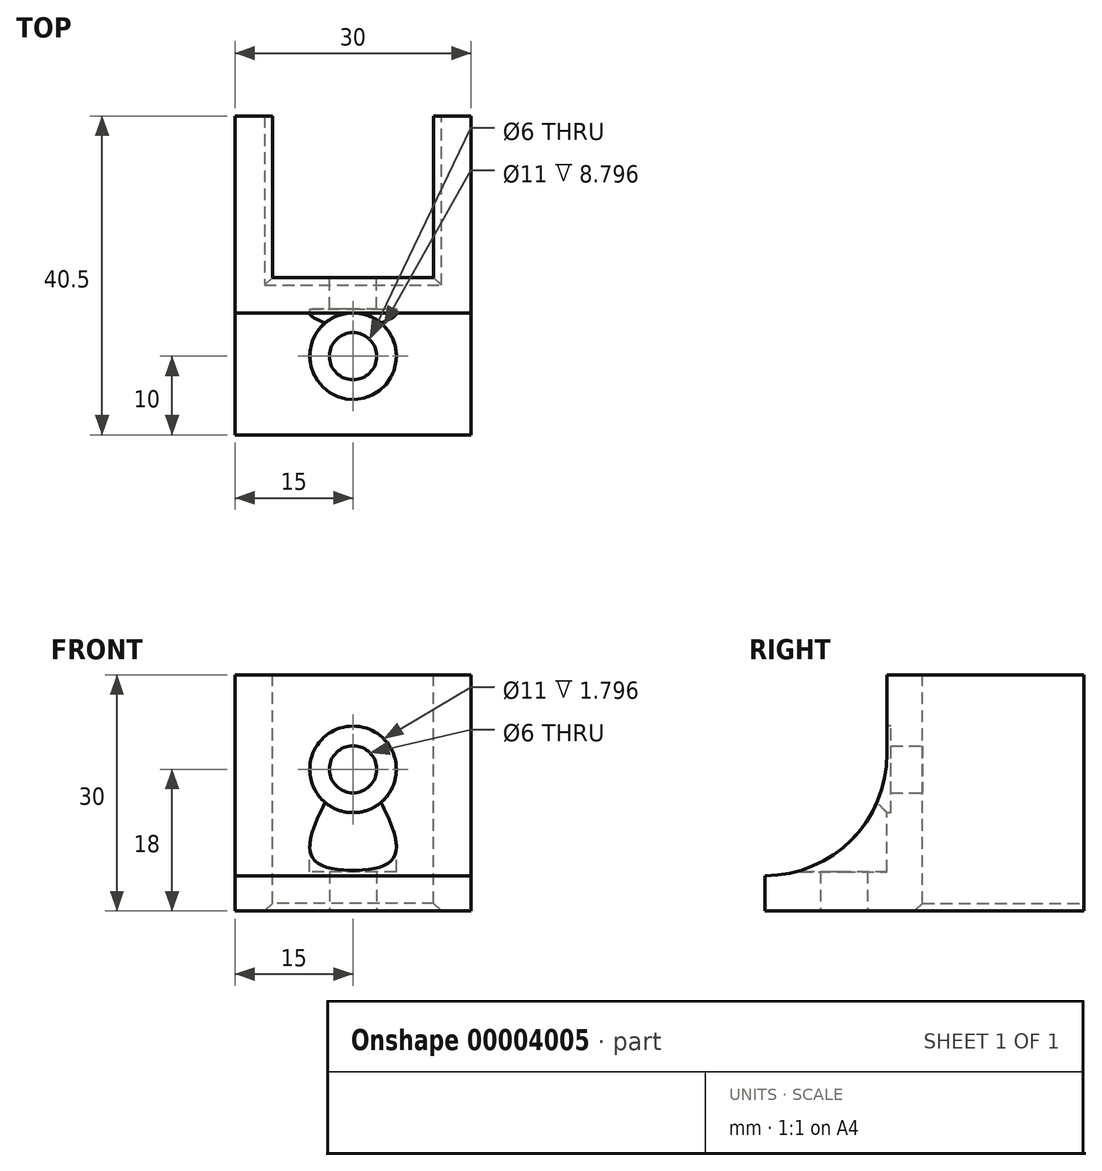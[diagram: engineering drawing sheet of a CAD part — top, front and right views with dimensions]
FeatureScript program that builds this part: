
annotation { "Feature Type Name" : "Feature", "Feature Type Description" : "" }
export const myFeature = defineFeature(function(context is Context, id is Id, definition is map)
    precondition{}
    {
        {
            var Q0;
            Q0=qCreatedBy(makeId("Top.planeOp"),FACE);
            var sketch = newSketch(context, id + "F0", { "sketchPlane" : qUnion([Q0])});
            skLineSegment(sketch, "E0", {"start": v(-15, 0) * mm, "end": v(15, 0) * mm});
            skLineSegment(sketch, "E1", {"start": v(15, 0) * mm, "end": v(15, 40.5) * mm});
            skLineSegment(sketch, "E2", {"start": v(15, 40.5) * mm, "end": v(-15, 40.5) * mm});
            skLineSegment(sketch, "E3", {"start": v(-15, 40.5) * mm, "end": v(-15, 0) * mm});
            skSolve(sketch);
        }
        {
            var Q0;
            Q0=makeQuery(id+"F0.imprint","IMPRINT",FACE,{"disambiguationData":[TD([[makeQuery(id+"F0.imprint","IMPRINT",EDGE,{"derivedFrom":sQuery(id+"F0.wireOp",EDGE,"E0")}),1.0]])]});
            extrude(context, id + "F1", {"entities" : qUnion([Q0]), "depth" : 30 * mm});
        }
        {
            var Q0;
            Q0=makeQuery(id+"F1.opExtrude","CAP_FACE",FACE,{"disambiguationData":[OSD([sQuery(id+"F0.wireOp",EDGE,"E0"),sQuery(id+"F0.wireOp",EDGE,"E1"),sQuery(id+"F0.wireOp",EDGE,"E2"),sQuery(id+"F0.wireOp",EDGE,"E3")])],"isStart":false});
            var sketch = newSketch(context, id + "F2", { "sketchPlane" : qUnion([Q0])});
            skLineSegment(sketch, "E4.bottom", {"start": v(-10.25, 40.5) * mm, "end": v(10.25, 40.5) * mm});
            skLineSegment(sketch, "E4.top", {"start": v(-10.25, 20) * mm, "end": v(10.25, 20) * mm});
            skLineSegment(sketch, "E4.left", {"start": v(-10.25, 40.5) * mm, "end": v(-10.25, 20) * mm});
            skLineSegment(sketch, "E4.right", {"start": v(10.25, 40.5) * mm, "end": v(10.25, 20) * mm});
            skLineSegment(sketch, "E5", {"start": v(0, 0) * mm, "end": v(0, 20) * mm, "construction": true});
            skSolve(sketch);
        }
        {
            var Q0;
            Q0=makeQuery(id+"F2.imprint","IMPRINT",FACE,{"disambiguationData":[TD([[makeQuery(id+"F2.imprint","IMPRINT",EDGE,{"derivedFrom":sQuery(id+"F2.wireOp",EDGE,"E4.bottom")}),1.0]])]});
            extrude(context, id + "F3", {"entities" : qUnion([Q0]), "operationType" : NewBodyOperationType.REMOVE, "endBound" : BoundingType.THROUGH_ALL, "oppositeDirection" : true, "depth" : 25 * mm});
        }
        {
            var Q0;
            Q0=makeQuery(id+"F1.opExtrude","CAP_FACE",FACE,{"disambiguationData":[OSD([sQuery(id+"F0.wireOp",EDGE,"E0"),sQuery(id+"F0.wireOp",EDGE,"E1"),sQuery(id+"F0.wireOp",EDGE,"E2"),sQuery(id+"F0.wireOp",EDGE,"E3")])],"isStart":true});
            var sketch = newSketch(context, id + "F4", { "sketchPlane" : qUnion([Q0])});
            skLineSegment(sketch, "E6", {"start": v(0, 0) * mm, "end": v(0, -10) * mm, "construction": true});
            skCircle(sketch, "E7", {"center": v(0, -10) * mm, "radius": 3 * mm});
            skSolve(sketch);
        }
        {
            var Q0;
            Q0=makeQuery(id+"F4.imprint","IMPRINT",FACE,{"disambiguationData":[TD([[makeQuery(id+"F4.imprint","IMPRINT",EDGE,{"derivedFrom":sQuery(id+"F4.wireOp",EDGE,"E7")}),1.0]])]});
            extrude(context, id + "F5", {"entities" : qUnion([Q0]), "operationType" : NewBodyOperationType.REMOVE, "endBound" : BoundingType.THROUGH_ALL, "oppositeDirection" : true, "depth" : 25 * mm});
        }
        {
            var Q0;
            Q0=makeQuery(id+"F3.boolean.opBoolean","COPY",FACE,{"derivedFrom":makeQuery(id+"F3.opExtrude","SWEPT_FACE",FACE,{"disambiguationData":[OSD([sQuery(id+"F2.wireOp",EDGE,"E4.top")])]})});
            var sketch = newSketch(context, id + "F6", { "sketchPlane" : qUnion([Q0])});
            skLineSegment(sketch, "E8", {"start": v(0, 30) * mm, "end": v(0, 18) * mm, "construction": true});
            skCircle(sketch, "E9", {"center": v(0, 18) * mm, "radius": 3 * mm});
            skSolve(sketch);
        }
        {
            var Q0;
            Q0=makeQuery(id+"F6.imprint","IMPRINT",FACE,{"disambiguationData":[TD([[makeQuery(id+"F6.imprint","IMPRINT",EDGE,{"derivedFrom":sQuery(id+"F6.wireOp",EDGE,"E9")}),1.0]])]});
            extrude(context, id + "F7", {"entities" : qUnion([Q0]), "operationType" : NewBodyOperationType.REMOVE, "endBound" : BoundingType.THROUGH_ALL, "oppositeDirection" : true, "depth" : 25 * mm});
        }
        {
            var Q0;
            Q0=makeQuery(id+"F1.opExtrude","CAP_FACE",FACE,{"disambiguationData":[OSD([sQuery(id+"F0.wireOp",EDGE,"E0"),sQuery(id+"F0.wireOp",EDGE,"E1"),sQuery(id+"F0.wireOp",EDGE,"E2"),sQuery(id+"F0.wireOp",EDGE,"E3")])],"isStart":false});
            var sketch = newSketch(context, id + "F8", { "sketchPlane" : qUnion([Q0])});
            skCircle(sketch, "E10", {"center": v(0, 10) * mm, "radius": 5.5 * mm});
            skSolve(sketch);
        }
        {
            var Q0;
            {var subQ0=makeQuery(id+"F8.imprint","IMPRINT",EDGE,{"derivedFrom":makeQuery(id+"F5.boolean.opBoolean","INTERSECT",EDGE,{"derivedFrom":[makeQuery(id+"F1.opExtrude","CAP_FACE",FACE,{"disambiguationData":[OSD([sQuery(id+"F0.wireOp",EDGE,"E0"),sQuery(id+"F0.wireOp",EDGE,"E1"),sQuery(id+"F0.wireOp",EDGE,"E2"),sQuery(id+"F0.wireOp",EDGE,"E3")])],"isStart":false}),makeQuery(id+"F5.opExtrude","SWEPT_FACE",FACE,{"disambiguationData":[OSD([sQuery(id+"F4.wireOp",EDGE,"E7")])]})]})});Q0=qUnion([makeQuery(id+"F8.imprint","IMPRINT",FACE,{"disambiguationData":[TD([[subQ0,1.0]])]}),makeQuery(id+"F8.imprint","IMPRINT",FACE,{"disambiguationData":[TD([[makeQuery(id+"F8.imprint","IMPRINT",EDGE,{"derivedFrom":sQuery(id+"F8.wireOp",EDGE,"E10")}),1.0]])]})]);}
            extrude(context, id + "F9", {"entities" : qUnion([Q0]), "operationType" : NewBodyOperationType.REMOVE, "oppositeDirection" : true, "depth" : 25 * mm});
        }
        {
            var Q0;
            Q0=makeQuery(id+"F1.opExtrude","SWEPT_FACE",FACE,{"disambiguationData":[OSD([sQuery(id+"F0.wireOp",EDGE,"E0")])]});
            var sketch = newSketch(context, id + "F10", { "sketchPlane" : qUnion([Q0])});
            skCircle(sketch, "E11", {"center": v(0, 18) * mm, "radius": 5.5 * mm});
            skSolve(sketch);
        }
        {
            var Q0;
            {var subQ0=makeQuery(id+"F10.imprint","IMPRINT",EDGE,{"derivedFrom":makeQuery(id+"F7.boolean.opBoolean","INTERSECT",EDGE,{"derivedFrom":[makeQuery(id+"F1.opExtrude","SWEPT_FACE",FACE,{"disambiguationData":[OSD([sQuery(id+"F0.wireOp",EDGE,"E0")])]}),makeQuery(id+"F7.opExtrude","SWEPT_FACE",FACE,{"disambiguationData":[OSD([sQuery(id+"F6.wireOp",EDGE,"E9")])]})]})});Q0=qUnion([makeQuery(id+"F10.imprint","IMPRINT",FACE,{"disambiguationData":[TD([[subQ0,-1.0]])]}),makeQuery(id+"F10.imprint","IMPRINT",FACE,{"disambiguationData":[TD([[makeQuery(id+"F10.imprint","IMPRINT",EDGE,{"derivedFrom":sQuery(id+"F10.wireOp",EDGE,"E11")}),1.0]])]})]);}
            extrude(context, id + "F11", {"entities" : qUnion([Q0]), "operationType" : NewBodyOperationType.REMOVE, "oppositeDirection" : true, "depth" : 16 * mm});
        }
        {
            var Q0;
            Q0=makeQuery(id+"F1.opExtrude","SWEPT_FACE",FACE,{"disambiguationData":[OSD([sQuery(id+"F0.wireOp",EDGE,"E1")])]});
            var sketch = newSketch(context, id + "F12", { "sketchPlane" : qUnion([Q0])});
            skLineSegment(sketch, "E12", {"start": v(15.5, 30) * mm, "end": v(15.5, 20) * mm});
            skArc(sketch, "E13", {"start": v(15.5, 20) * mm, "mid": v(10.96, 9.04) * mm, "end": v(0, 4.5) * mm});
            skLineSegment(sketch, "E14", {"start": v(15.5, 30) * mm, "end": v(0, 30) * mm});
            skLineSegment(sketch, "E15", {"start": v(0, 30) * mm, "end": v(0, 4.5) * mm});
            skSolve(sketch);
        }
        {
            var Q0;
            Q0=makeQuery(id+"F12.imprint","IMPRINT",FACE,{"disambiguationData":[TD([[makeQuery(id+"F12.imprint","IMPRINT",EDGE,{"derivedFrom":sQuery(id+"F12.wireOp",EDGE,"E12")}),-1.0]])]});
            extrude(context, id + "F13", {"entities" : qUnion([Q0]), "operationType" : NewBodyOperationType.REMOVE, "endBound" : BoundingType.THROUGH_ALL, "oppositeDirection" : true, "depth" : 25 * mm});
        }
        {
            var Q0;
            Q0=makeQuery(id+"F3.boolean.opBoolean","INTERSECT",EDGE,{"derivedFrom":[makeQuery(id+"F1.opExtrude","CAP_FACE",FACE,{"disambiguationData":[OSD([sQuery(id+"F0.wireOp",EDGE,"E0"),sQuery(id+"F0.wireOp",EDGE,"E1"),sQuery(id+"F0.wireOp",EDGE,"E2"),sQuery(id+"F0.wireOp",EDGE,"E3")])],"isStart":true}),makeQuery(id+"F3.opExtrude","SWEPT_FACE",FACE,{"disambiguationData":[OSD([sQuery(id+"F2.wireOp",EDGE,"E4.top")])]})]});
            var Q1;
            Q1=makeQuery(id+"F3.boolean.opBoolean","INTERSECT",EDGE,{"derivedFrom":[makeQuery(id+"F1.opExtrude","CAP_FACE",FACE,{"disambiguationData":[OSD([sQuery(id+"F0.wireOp",EDGE,"E0"),sQuery(id+"F0.wireOp",EDGE,"E1"),sQuery(id+"F0.wireOp",EDGE,"E2"),sQuery(id+"F0.wireOp",EDGE,"E3")])],"isStart":true}),makeQuery(id+"F3.opExtrude","SWEPT_FACE",FACE,{"disambiguationData":[OSD([sQuery(id+"F2.wireOp",EDGE,"E4.right")])]})]});
            var Q2;
            Q2=makeQuery(id+"F3.boolean.opBoolean","INTERSECT",EDGE,{"derivedFrom":[makeQuery(id+"F1.opExtrude","CAP_FACE",FACE,{"disambiguationData":[OSD([sQuery(id+"F0.wireOp",EDGE,"E0"),sQuery(id+"F0.wireOp",EDGE,"E1"),sQuery(id+"F0.wireOp",EDGE,"E2"),sQuery(id+"F0.wireOp",EDGE,"E3")])],"isStart":true}),makeQuery(id+"F3.opExtrude","SWEPT_FACE",FACE,{"disambiguationData":[OSD([sQuery(id+"F2.wireOp",EDGE,"E4.left")])]})]});
            chamfer(context, id + "F14", {"entities" : qUnion([Q0, Q1, Q2]), "width" : 1 * mm, "tangentPropagation" : true});
        }
    });
